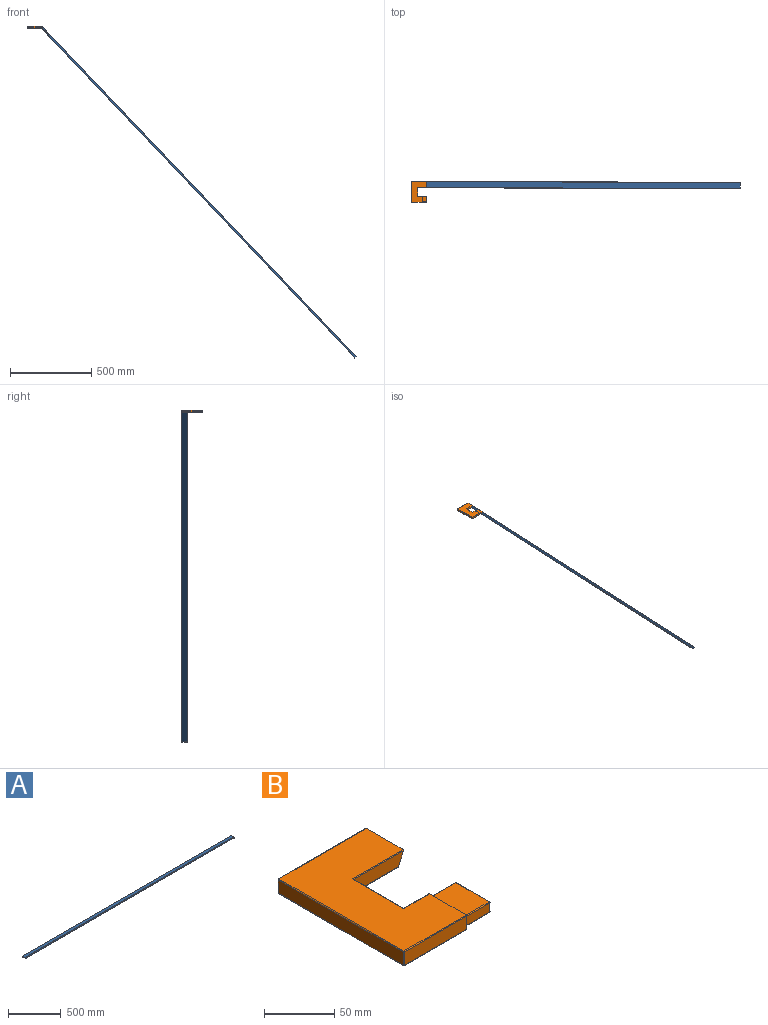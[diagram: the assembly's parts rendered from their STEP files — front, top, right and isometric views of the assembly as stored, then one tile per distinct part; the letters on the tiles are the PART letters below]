
ASSEMBLY  parts=2 mates=1
PART A: 19 faces, bbox 2800.4x38.1x12.8 mm
  f0: plane 2794.26x36.83mm, normal (0,0,-1), area 102922.9mm2, adj f6,f10,f11,f13
  f1: plane 2799.47x11.49mm, normal (0,1,0), area 32149.5mm2, adj f7,f10,f13,f15
  f2: plane 2799.72x36.83mm, normal (0,0,1), area 103123.7mm2, adj f5,f9,f15,f17
  f3: plane 2799.47x11.49mm, normal (0,-1,0), area 32149.5mm2, adj f8,f10,f11,f17
  f4: plane 36.83x11.49mm, normal (1,0,0), area 423.4mm2, adj f6,f7,f8,f9
  f5: plane 37.39x0.06mm, normal (-1,0,0), area 2.4mm2, adj f2,f10,f15,f17
  f6: cylinder r=0.64mm len=36.83mm, axis (0,-1,0), area 36.7mm2, adj f0,f4,f12,f14
  f7: cylinder r=0.64mm len=11.49mm, axis (0,0,-1), area 11.5mm2, adj f1,f4,f14,f16
  f8: cylinder r=0.64mm len=11.49mm, axis (0,0,1), area 11.5mm2, adj f3,f4,f12,f18
  f9: cylinder r=0.64mm len=36.83mm, axis (0,1,0), area 36.7mm2, adj f2,f4,f16,f18
  f10: plane 38.1x12.7mm, normal (-0.92,0,-0.39), area 526.3mm2, adj f0,f1,f3,f5,f11,f13,f15,f17
  f11: cylinder r=0.64mm len=2794.54mm, axis (-1,0,0), area 2787.3mm2, adj f0,f3,f10,f12
  f12: sphere r=0.64mm, area 0.6mm2, adj f6,f8,f11
  f13: cylinder r=0.64mm len=2794.54mm, axis (1,0,0), area 2787.3mm2, adj f0,f1,f10,f14
  f14: sphere r=0.64mm, area 0.6mm2, adj f6,f7,f13
  f15: cylinder r=0.64mm len=2799.72mm, axis (-1,0,0), area 2792.5mm2, adj f1,f2,f5,f10,f16
  f16: sphere r=0.64mm, area 0.6mm2, adj f7,f9,f15
  f17: cylinder r=0.64mm len=2799.72mm, axis (1,0,0), area 2792.5mm2, adj f2,f3,f5,f10,f18
  f18: sphere r=0.64mm, area 0.6mm2, adj f8,f9,f17
PART B: 45 faces, bbox 88.9x127.1x12.7 mm
  f0: plane 38.25x12.7mm, normal (1,0,0), area 168.5mm2, adj f3,f4,f7,f8,f9,f10,f11,f12
  f1: plane 87.96x11.43mm, normal (0,1,0), area 977.3mm2, adj f26,f35,f38,f41
  f2: plane 125.84x11.43mm, normal (-1,0,0), area 1438.4mm2, adj f31,f36,f37,f41
  f3: plane 62.84x11.43mm, normal (0,-1,0), area 718.2mm2, adj f0,f30,f31,f32
  f4: plane 25.39x11.43mm, normal (0,1,0), area 290.2mm2, adj f0,f5,f27,f42
  f5: plane 50.78x11.43mm, normal (1,0,0), area 580.4mm2, adj f4,f6,f28,f43
  f6: plane 50.51x11.43mm, normal (0,-1,0), area 549.2mm2, adj f5,f26,f29,f44
  f7: plane 125.84x88.23mm, normal (0,0,1), area 7488mm2, adj f0,f26,f30,f35,f36,f42,f43,f44
  f8: plane 125.84x82.78mm, normal (0,0,-1), area 7287.3mm2, adj f0,f26,f27,f28,f29,f32,f37,f38
  f9: plane 33.43x24.77mm, normal (0,0,-1), area 827.8mm2, adj f0,f16,f22,f25
  f10: plane 24.77x7.87mm, normal (0,1,0), area 195mm2, adj f0,f19,f23,f25
  f11: plane 33.43x24.77mm, normal (0,0,1), area 827.8mm2, adj f0,f14,f18,f19
  f12: plane 24.77x7.87mm, normal (0,-1,0), area 195mm2, adj f0,f14,f16,f17
  f13: plane 33.43x7.87mm, normal (1,0,0), area 263.2mm2, adj f17,f18,f22,f23
  f14: cylinder r=0.64mm len=24.77mm, axis (-1,0,0), area 24.7mm2, adj f0,f11,f12,f15
  f15: sphere r=0.64mm, area 0.6mm2, adj f14,f17,f18
  f16: cylinder r=0.64mm len=24.77mm, axis (-1,0,0), area 24.7mm2, adj f0,f9,f12,f20
  f17: cylinder r=0.64mm len=7.87mm, axis (0,0,1), area 7.9mm2, adj f12,f13,f15,f20
  f18: cylinder r=0.64mm len=33.43mm, axis (0,1,0), area 33.3mm2, adj f11,f13,f15,f21
  f19: cylinder r=0.64mm len=24.77mm, axis (-1,0,0), area 24.7mm2, adj f0,f10,f11,f21
  f20: sphere r=0.64mm, area 0.6mm2, adj f16,f17,f22
  f21: sphere r=0.64mm, area 0.6mm2, adj f18,f19,f23
  f22: cylinder r=0.64mm len=33.43mm, axis (0,-1,0), area 33.3mm2, adj f9,f13,f20,f24
  f23: cylinder r=0.64mm len=7.87mm, axis (0,0,-1), area 7.9mm2, adj f10,f13,f21,f24
  f24: sphere r=0.64mm, area 0.6mm2, adj f22,f23,f25
  f25: cylinder r=0.64mm len=24.77mm, axis (-1,0,0), area 24.7mm2, adj f0,f9,f10,f24
  f26: plane 38.08x12.7mm, normal (0.92,0,-0.39), area 526mm2, adj f1,f6,f7,f8,f29,f35,f38,f44
  f27: cylinder r=0.64mm len=26.02mm, axis (-1,0,0), area 25.6mm2, adj f0,f4,f8,f28
  f28: cylinder r=0.64mm len=52.05mm, axis (0,1,0), area 51.1mm2, adj f5,f8,f27,f29
  f29: cylinder r=0.64mm len=46.23mm, axis (1,0,0), area 45.5mm2, adj f6,f8,f26,f28
  f30: cylinder r=0.64mm len=62.84mm, axis (-1,0,0), area 62.7mm2, adj f0,f3,f7,f33
  f31: cylinder r=0.64mm len=11.43mm, axis (0,0,1), area 11.4mm2, adj f2,f3,f33,f34
  f32: cylinder r=0.64mm len=62.84mm, axis (1,0,0), area 62.7mm2, adj f0,f3,f8,f34
  f33: sphere r=0.64mm, area 0.6mm2, adj f30,f31,f36
  f34: sphere r=0.64mm, area 0.6mm2, adj f31,f32,f37
  f35: cylinder r=0.64mm len=88.23mm, axis (1,0,0), area 87.9mm2, adj f1,f7,f26,f39
  f36: cylinder r=0.64mm len=125.84mm, axis (0,1,0), area 125.5mm2, adj f2,f7,f33,f39
  f37: cylinder r=0.64mm len=125.84mm, axis (0,-1,0), area 125.5mm2, adj f2,f8,f34,f40
  f38: cylinder r=0.64mm len=83.05mm, axis (-1,0,0), area 82.7mm2, adj f1,f8,f26,f40
  f39: sphere r=0.64mm, area 0.6mm2, adj f35,f36,f41
  f40: sphere r=0.64mm, area 0.6mm2, adj f37,f38,f41
  f41: cylinder r=0.64mm len=11.43mm, axis (0,0,1), area 11.4mm2, adj f1,f2,f39,f40
  f42: cylinder r=0.64mm len=26.02mm, axis (1,0,0), area 25.6mm2, adj f0,f4,f7,f43
  f43: cylinder r=0.64mm len=52.05mm, axis (0,-1,0), area 51.1mm2, adj f5,f7,f42,f44
  f44: cylinder r=0.64mm len=51.41mm, axis (-1,0,0), area 50.8mm2, adj f6,f7,f26,f43
PLACE A rot(axis=(0,1,0),46.5deg) t=(838.77,316.7,1114.1)mm
PLACE B t=(805.77,274.89,1105.8)mm
MATE parallel B.f26 <-> A.f10  axis (0.92,0,-0.39) through (840.67,316.7,1112.15)mm
